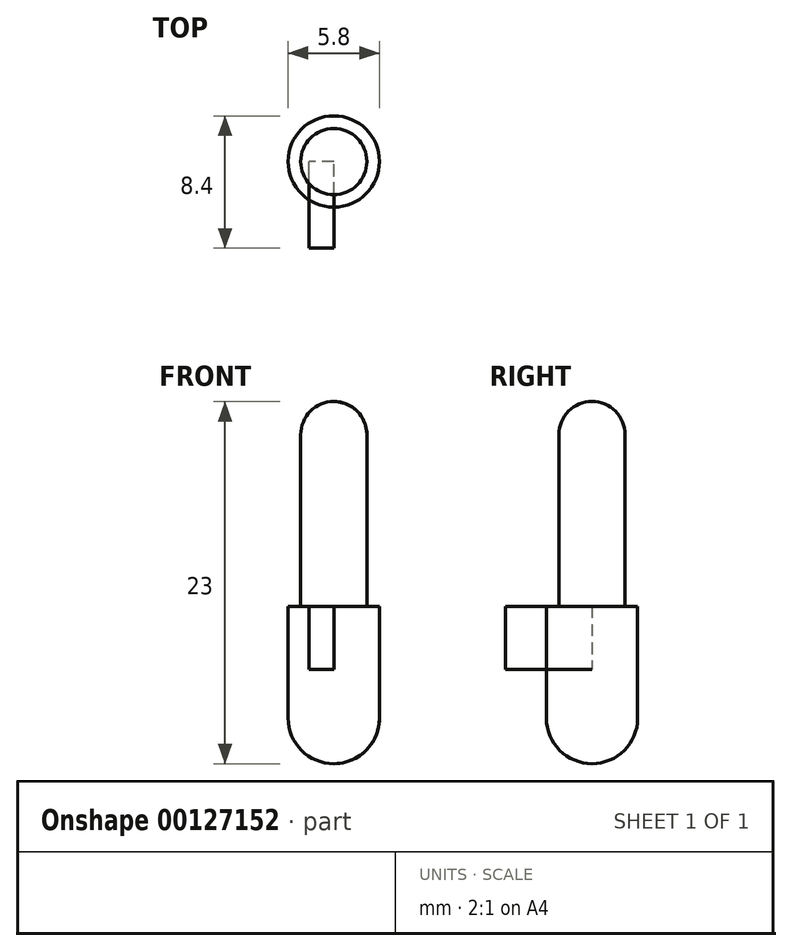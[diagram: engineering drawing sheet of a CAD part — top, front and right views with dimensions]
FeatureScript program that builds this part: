
annotation { "Feature Type Name" : "Feature", "Feature Type Description" : "" }
export const myFeature = defineFeature(function(context is Context, id is Id, definition is map)
    precondition{}
    {
        {
            var Q0;
            Q0=qCreatedBy(makeId("Top.planeOp"),FACE);
            var sketch = newSketch(context, id + "F0", { "sketchPlane" : qUnion([Q0])});
            skCircle(sketch, "E0", {"center": v(0, 0) * mm, "radius": 2.9 * mm});
            skCircle(sketch, "E1", {"center": v(0, 0) * mm, "radius": 2.1 * mm});
            skSolve(sketch);
        }
        {
            var Q0;
            Q0=makeQuery(id+"F0.imprint","IMPRINT",FACE,{"disambiguationData":[TD([[makeQuery(id+"F0.imprint","IMPRINT",EDGE,{"derivedFrom":sQuery(id+"F0.wireOp",EDGE,"E1")}),1.0]])]});
            extrude(context, id + "F1", {"entities" : qUnion([Q0]), "depth" : 13 * mm});
        }
        {
            var Q0;
            Q0=makeQuery(id+"F0.imprint","IMPRINT",FACE,{"disambiguationData":[TD([[makeQuery(id+"F0.imprint","IMPRINT",EDGE,{"derivedFrom":sQuery(id+"F0.wireOp",EDGE,"E0")}),1.0]])]});
            var Q1;
            Q1=makeQuery(id+"F0.imprint","IMPRINT",FACE,{"disambiguationData":[TD([[makeQuery(id+"F0.imprint","IMPRINT",EDGE,{"derivedFrom":sQuery(id+"F0.wireOp",EDGE,"E1")}),1.0]])]});
            extrude(context, id + "F2", {"entities" : qUnion([Q0, Q1]), "operationType" : NewBodyOperationType.ADD, "oppositeDirection" : true, "depth" : 10 * mm});
        }
        {
            var Q0;
            Q0=makeQuery(id+"F1.opExtrude","CAP_EDGE",EDGE,{"disambiguationData":[OSD([sQuery(id+"F0.wireOp",EDGE,"E1")])],"isStart":false});
            fillet(context, id + "F3", {"entities" : qUnion([Q0]), "radius" : 2.1 * mm, "tangentPropagation" : true, "allowEdgeOverflow" : false});
        }
        {
            var Q0;
            Q0=makeQuery(id+"F2.opExtrude","CAP_EDGE",EDGE,{"disambiguationData":[OSD([sQuery(id+"F0.wireOp",EDGE,"E0")])],"isStart":false});
            fillet(context, id + "F4", {"entities" : qUnion([Q0]), "radius" : 2.9 * mm, "tangentPropagation" : true, "allowEdgeOverflow" : false});
        }
        {
            var Q0;
            Q0=qCreatedBy(makeId("Front.planeOp"),FACE);
            var sketch = newSketch(context, id + "F5", { "sketchPlane" : qUnion([Q0])});
            skLineSegment(sketch, "E2", {"start": v(2.9, 0) * mm, "end": v(2.9, -7.1) * mm});
            skLineSegment(sketch, "E3", {"start": v(-2.9, -7.1) * mm, "end": v(-2.9, 0) * mm});
            skLineSegment(sketch, "E4.bottom", {"start": v(0, 0) * mm, "end": v(-1.56, 0) * mm});
            skLineSegment(sketch, "E4.top", {"start": v(0, -4) * mm, "end": v(-1.56, -4) * mm});
            skLineSegment(sketch, "E4.left", {"start": v(0, 0) * mm, "end": v(0, -4) * mm});
            skLineSegment(sketch, "E4.right", {"start": v(-1.56, 0) * mm, "end": v(-1.56, -4) * mm});
            skSolve(sketch);
        }
        {
            var Q0;
            Q0 = qSketchRegion(id + "F5", true);
            var Q1;
            Q1=sQuery(id+"F5.wireOp",EDGE,"E4.right");
            var Q2;
            Q2=sQuery(id+"F5.wireOp",EDGE,"E4.bottom");
            var Q3;
            Q3=sQuery(id+"F5.wireOp",EDGE,"E4.left");
            var Q4;
            Q4=sQuery(id+"F5.wireOp",EDGE,"E4.top");
            extrude(context, id + "F6", {"entities" : qUnion([Q0]), "surfaceEntities" : qUnion([Q1, Q2, Q3, Q4]), "depth" : 5.5 * mm});
        }
    });
